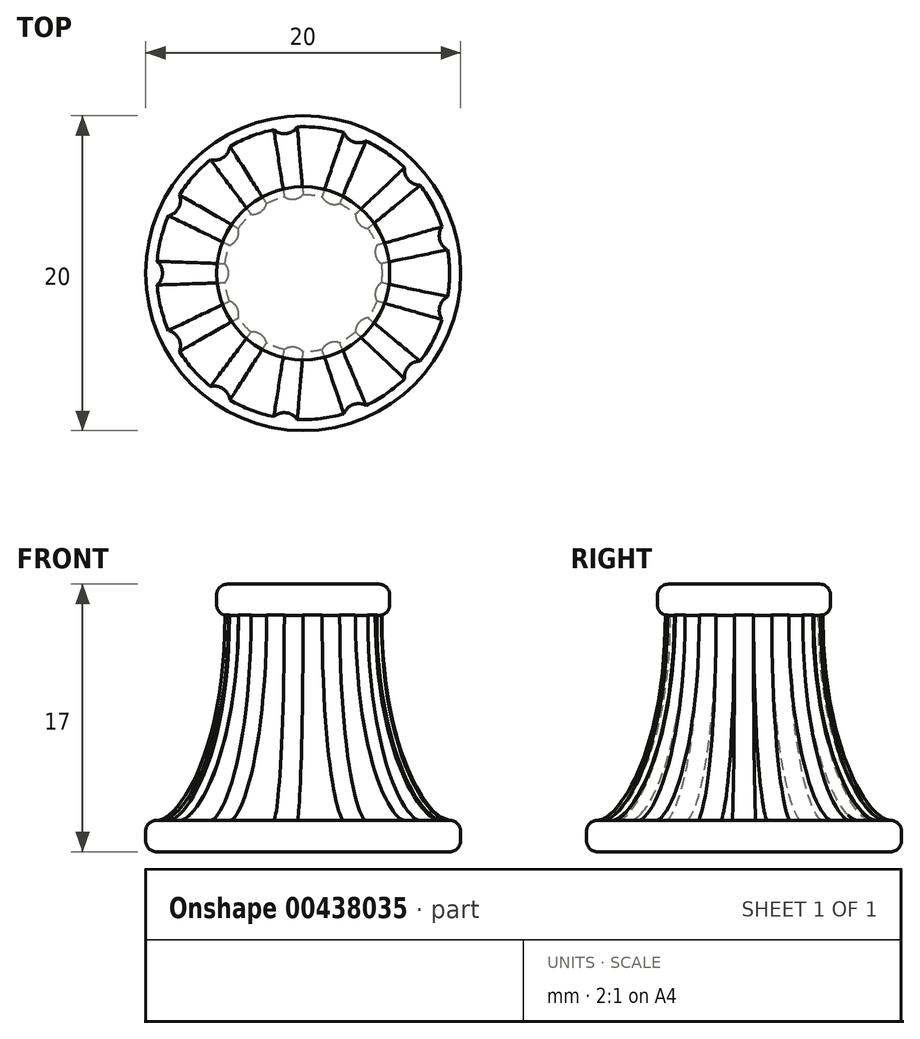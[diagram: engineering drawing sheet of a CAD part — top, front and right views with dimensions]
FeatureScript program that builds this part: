
annotation { "Feature Type Name" : "Feature", "Feature Type Description" : "" }
export const myFeature = defineFeature(function(context is Context, id is Id, definition is map)
    precondition{}
    {
        {
            var Q0;
            Q0=qCreatedBy(makeId("Top.planeOp"),FACE);
            var sketch = newSketch(context, id + "F0", { "sketchPlane" : qUnion([Q0])});
            skCircle(sketch, "E0", {"center": v(0, 0) * mm, "radius": 10 * mm});
            skSolve(sketch);
        }
        {
            var Q0;
            Q0=makeQuery(id+"F0.imprint","IMPRINT",FACE,{"disambiguationData":[TD([[makeQuery(id+"F0.imprint","IMPRINT",EDGE,{"derivedFrom":sQuery(id+"F0.wireOp",EDGE,"E0")}),1.0]])]});
            extrude(context, id + "F1", {"entities" : qUnion([Q0]), "depth" : 2 * mm});
        }
        {
            var Q0;
            Q0=makeQuery(id+"F1.opExtrude","SWEPT_FACE",FACE,{"disambiguationData":[OSD([sQuery(id+"F0.wireOp",EDGE,"E0")])]});
            fillet(context, id + "F2", {"entities" : qUnion([Q0]), "radius" : 0.7 * mm, "tangentPropagation" : true, "allowEdgeOverflow" : false});
        }
        {
            var Q0;
            Q0=makeQuery(id+"F1.opExtrude","CAP_FACE",FACE,{"disambiguationData":[OSD([sQuery(id+"F0.wireOp",EDGE,"E0")])],"isStart":false});
            var sketch = newSketch(context, id + "F3", { "sketchPlane" : qUnion([Q0])});
            skArc(sketch, "E1", {"start": v(-9.27, -0.75) * mm, "mid": v(-8.93, 0) * mm, "end": v(-9.27, 0.75) * mm});
            skArc(sketch, "E2.1.0", {"start": v(-7.86, -4.97) * mm, "mid": v(-7.9, -4.15) * mm, "end": v(-8.56, -3.64) * mm});
            skArc(sketch, "E2.2.0", {"start": v(-4.65, -8.05) * mm, "mid": v(-5.07, -7.35) * mm, "end": v(-5.88, -7.2) * mm});
            skArc(sketch, "E2.3.0", {"start": v(-0.37, -9.3) * mm, "mid": v(-1.08, -8.87) * mm, "end": v(-1.86, -9.11) * mm});
            skArc(sketch, "E2.4.0", {"start": v(3.99, -8.4) * mm, "mid": v(3.17, -8.35) * mm, "end": v(2.59, -8.93) * mm});
            skArc(sketch, "E2.5.0", {"start": v(7.44, -5.59) * mm, "mid": v(6.69, -5.92) * mm, "end": v(6.44, -6.7) * mm});
            skArc(sketch, "E2.6.0", {"start": v(9.18, -1.5) * mm, "mid": v(8.67, -2.14) * mm, "end": v(8.82, -2.95) * mm});
            skArc(sketch, "E2.7.0", {"start": v(8.82, 2.95) * mm, "mid": v(8.67, 2.14) * mm, "end": v(9.18, 1.5) * mm});
            skArc(sketch, "E2.8.0", {"start": v(6.44, 6.7) * mm, "mid": v(6.69, 5.92) * mm, "end": v(7.44, 5.59) * mm});
            skArc(sketch, "E2.9.0", {"start": v(2.59, 8.93) * mm, "mid": v(3.17, 8.35) * mm, "end": v(3.99, 8.4) * mm});
            skArc(sketch, "E2.10.0", {"start": v(-1.86, 9.11) * mm, "mid": v(-1.08, 8.87) * mm, "end": v(-0.37, 9.3) * mm});
            skArc(sketch, "E2.11.0", {"start": v(-5.88, 7.2) * mm, "mid": v(-5.07, 7.35) * mm, "end": v(-4.65, 8.05) * mm});
            skArc(sketch, "E2.12.0", {"start": v(-8.56, 3.64) * mm, "mid": v(-7.9, 4.15) * mm, "end": v(-7.86, 4.97) * mm});
            skPoint(sketch, "E2.center", {"position": v(0, 0) * mm});
            skSolve(sketch);
        }
        {
            var Q0;
            Q0=qCreatedBy(makeId("Top.planeOp"),FACE);
            cPlane(context, id + "F4", {"entities" : qUnion([Q0]), "cplaneType" : CPlaneType.OFFSET, "offset" : 15 * mm, "width" : 150 * mm, "height" : 150 * mm});
        }
        {
            var Q0;
            Q0=qCreatedBy(id+"F4.planeOp",FACE);
            var sketch = newSketch(context, id + "F5", { "sketchPlane" : qUnion([Q0])});
            skArc(sketch, "E3", {"start": v(-4.96, -0.6) * mm, "mid": v(-4.73, 0) * mm, "end": v(-4.96, 0.6) * mm});
            skArc(sketch, "E4.1.0", {"start": v(-4.12, -2.84) * mm, "mid": v(-4.2, -2.2) * mm, "end": v(-4.67, -1.78) * mm});
            skArc(sketch, "E4.2.0", {"start": v(-2.33, -4.43) * mm, "mid": v(-2.69, -3.9) * mm, "end": v(-3.31, -3.74) * mm});
            skArc(sketch, "E4.3.0", {"start": v(0, -5) * mm, "mid": v(-0.57, -4.7) * mm, "end": v(-1.2, -4.86) * mm});
            skArc(sketch, "E4.4.0", {"start": v(2.32, -4.43) * mm, "mid": v(1.68, -4.43) * mm, "end": v(1.2, -4.85) * mm});
            skArc(sketch, "E4.5.0", {"start": v(4.11, -2.84) * mm, "mid": v(3.54, -3.14) * mm, "end": v(3.32, -3.74) * mm});
            skArc(sketch, "E4.6.0", {"start": v(4.96, -0.6) * mm, "mid": v(4.6, -1.13) * mm, "end": v(4.68, -1.77) * mm});
            skArc(sketch, "E4.7.0", {"start": v(4.68, 1.77) * mm, "mid": v(4.6, 1.13) * mm, "end": v(4.96, 0.6) * mm});
            skArc(sketch, "E4.8.0", {"start": v(3.32, 3.74) * mm, "mid": v(3.54, 3.14) * mm, "end": v(4.11, 2.84) * mm});
            skArc(sketch, "E4.9.0", {"start": v(1.2, 4.85) * mm, "mid": v(1.68, 4.43) * mm, "end": v(2.32, 4.43) * mm});
            skArc(sketch, "E4.10.0", {"start": v(-1.2, 4.86) * mm, "mid": v(-0.57, 4.7) * mm, "end": v(0, 5) * mm});
            skArc(sketch, "E4.11.0", {"start": v(-3.31, 3.74) * mm, "mid": v(-2.69, 3.9) * mm, "end": v(-2.33, 4.43) * mm});
            skArc(sketch, "E4.12.0", {"start": v(-4.67, 1.78) * mm, "mid": v(-4.2, 2.2) * mm, "end": v(-4.12, 2.84) * mm});
            skPoint(sketch, "E4.center", {"position": v(0, 0) * mm});
            skArc(sketch, "E5", {"start": v(-4.67, 1.78) * mm, "mid": v(-4.85, 1.2) * mm, "end": v(-4.96, 0.6) * mm});
            skArc(sketch, "E6.1.0", {"start": v(-4.96, -0.6) * mm, "mid": v(-4.85, -1.2) * mm, "end": v(-4.67, -1.78) * mm});
            skArc(sketch, "E6.2.0", {"start": v(-4.12, -2.84) * mm, "mid": v(-3.74, -3.32) * mm, "end": v(-3.31, -3.74) * mm});
            skArc(sketch, "E6.3.0", {"start": v(-2.33, -4.43) * mm, "mid": v(-1.77, -4.68) * mm, "end": v(-1.2, -4.86) * mm});
            skArc(sketch, "E6.4.0", {"start": v(0, -5) * mm, "mid": v(0.6, -4.96) * mm, "end": v(1.2, -4.85) * mm});
            skArc(sketch, "E6.5.0", {"start": v(2.32, -4.43) * mm, "mid": v(2.84, -4.11) * mm, "end": v(3.32, -3.74) * mm});
            skArc(sketch, "E6.6.0", {"start": v(4.11, -2.84) * mm, "mid": v(4.43, -2.32) * mm, "end": v(4.68, -1.77) * mm});
            skArc(sketch, "E6.7.0", {"start": v(4.96, -0.6) * mm, "mid": v(5, 0) * mm, "end": v(4.96, 0.6) * mm});
            skArc(sketch, "E6.8.0", {"start": v(4.68, 1.77) * mm, "mid": v(4.43, 2.32) * mm, "end": v(4.11, 2.84) * mm});
            skArc(sketch, "E6.9.0", {"start": v(3.32, 3.74) * mm, "mid": v(2.84, 4.11) * mm, "end": v(2.32, 4.43) * mm});
            skArc(sketch, "E6.10.0", {"start": v(1.2, 4.85) * mm, "mid": v(0.6, 4.96) * mm, "end": v(0, 5) * mm});
            skArc(sketch, "E6.11.0", {"start": v(-1.2, 4.86) * mm, "mid": v(-1.77, 4.68) * mm, "end": v(-2.33, 4.43) * mm});
            skArc(sketch, "E6.12.0", {"start": v(-3.31, 3.74) * mm, "mid": v(-3.74, 3.32) * mm, "end": v(-4.12, 2.84) * mm});
            skSolve(sketch);
        }
        {
            var Q1;
            {var subQ6=sQuery(id+"F3.wireOp",EDGE,"E1");Q1=makeQuery(id+"F3.imprint","IMPRINT",FACE,{"disambiguationData":[TD([[makeQuery(id+"F3.imprint","IMPRINT",EDGE,{"derivedFrom":subQ6}),-1.0]])]});}
            var Q2;
            Q2=makeQuery(id+"F5.imprint","IMPRINT",FACE,{"disambiguationData":[TD([[makeQuery(id+"F5.imprint","IMPRINT",EDGE,{"derivedFrom":sQuery(id+"F5.wireOp",EDGE,"E3")}),-1.0]])]});
            loft(context, id + "F6", {"operationType" : NewBodyOperationType.ADD, "startCondition" : LoftEndDerivativeType.TANGENT_TO_PROFILE, "startMagnitude" : 0.9, "endCondition" : LoftEndDerivativeType.NORMAL_TO_PROFILE, "endMagnitude" : 2, "sheetProfilesArray" : [{ "sheetProfileEntities" : qUnion([Q1]) }, { "sheetProfileEntities" : qUnion([Q2]) }]});
        }
        {
            var Q0;
            Q0=makeQuery(id+"F6.opLoft","CAP_FACE",FACE,{"disambiguationData":[OSD([makeQuery(id+"F5.imprint","IMPRINT",FACE,{"disambiguationData":[TD([[makeQuery(id+"F5.imprint","IMPRINT",EDGE,{"derivedFrom":sQuery(id+"F5.wireOp",EDGE,"E3")}),-1.0]])]})])],"isStart":true});
            var sketch = newSketch(context, id + "F7", { "sketchPlane" : qUnion([Q0])});
            skCircle(sketch, "E7", {"center": v(0, 0) * mm, "radius": 5.5 * mm});
            skSolve(sketch);
        }
        {
            var Q0;
            Q0=makeQuery(id+"F7.imprint","IMPRINT",FACE,{"disambiguationData":[TD([[makeQuery(id+"F7.imprint","IMPRINT",EDGE,{"derivedFrom":sQuery(id+"F7.wireOp",EDGE,"E7")}),1.0]])]});
            var Q1;
            {var subQ15=sQuery(id+"F5.wireOp",EDGE,"E6.1.0");var subQ17=sQuery(id+"F5.wireOp",EDGE,"E5");var subQ19=sQuery(id+"F5.wireOp",EDGE,"E3");Q1=makeQuery(id+"F7.imprint","IMPRINT",FACE,{"disambiguationData":[TD([[makeQuery(id+"F7.imprint","IMPRINT",EDGE,{"derivedFrom":makeQuery(id+"F6.opLoft","MID_CAP_EDGE",EDGE,{"disambiguationData":[OSD([subQ19,subQ17,subQ15])],"capPos":1.0})}),1.0]])]});}
            extrude(context, id + "F8", {"entities" : qUnion([Q0, Q1]), "operationType" : NewBodyOperationType.ADD, "depth" : 2 * mm});
        }
        {
            var Q0;
            Q0=makeQuery(id+"F8.opExtrude","SWEPT_FACE",FACE,{"disambiguationData":[OSD([sQuery(id+"F7.wireOp",EDGE,"E7")])]});
            fillet(context, id + "F9", {"entities" : qUnion([Q0]), "radius" : .7 * mm, "tangentPropagation" : true, "allowEdgeOverflow" : false});
        }
    });
